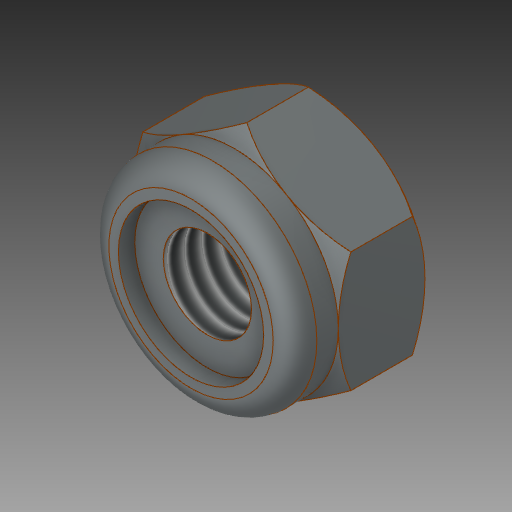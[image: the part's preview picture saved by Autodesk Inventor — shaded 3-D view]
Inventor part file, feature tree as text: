
AUTODESK INVENTOR PART (.ipt)
format: ipt  version: 2017.1 (Build 211199000, 199)  size: 201,728 bytes
history: native  units: in
note: dims shown in document units (in); Inventor stores cm internally (conversion verified against a paired STEP export)
features: thread x1, fillet x1
ambient origin geometry x8: Origin, YZ Plane, XZ Plane, XY Plane, X Axis, Y Axis, Z Axis, Center Point
bodies: Solid1 (feature_tree)
feature tree (2):
  thread  "Thread1"  [1 undecoded]
  fillet  "Fillet1"  [1 undecoded]
note: 2 required parameter values undecoded (feature->parameter linkage not recoverable at this tier; creation-order binding heuristic only, values carry confidence <= 0.55)
